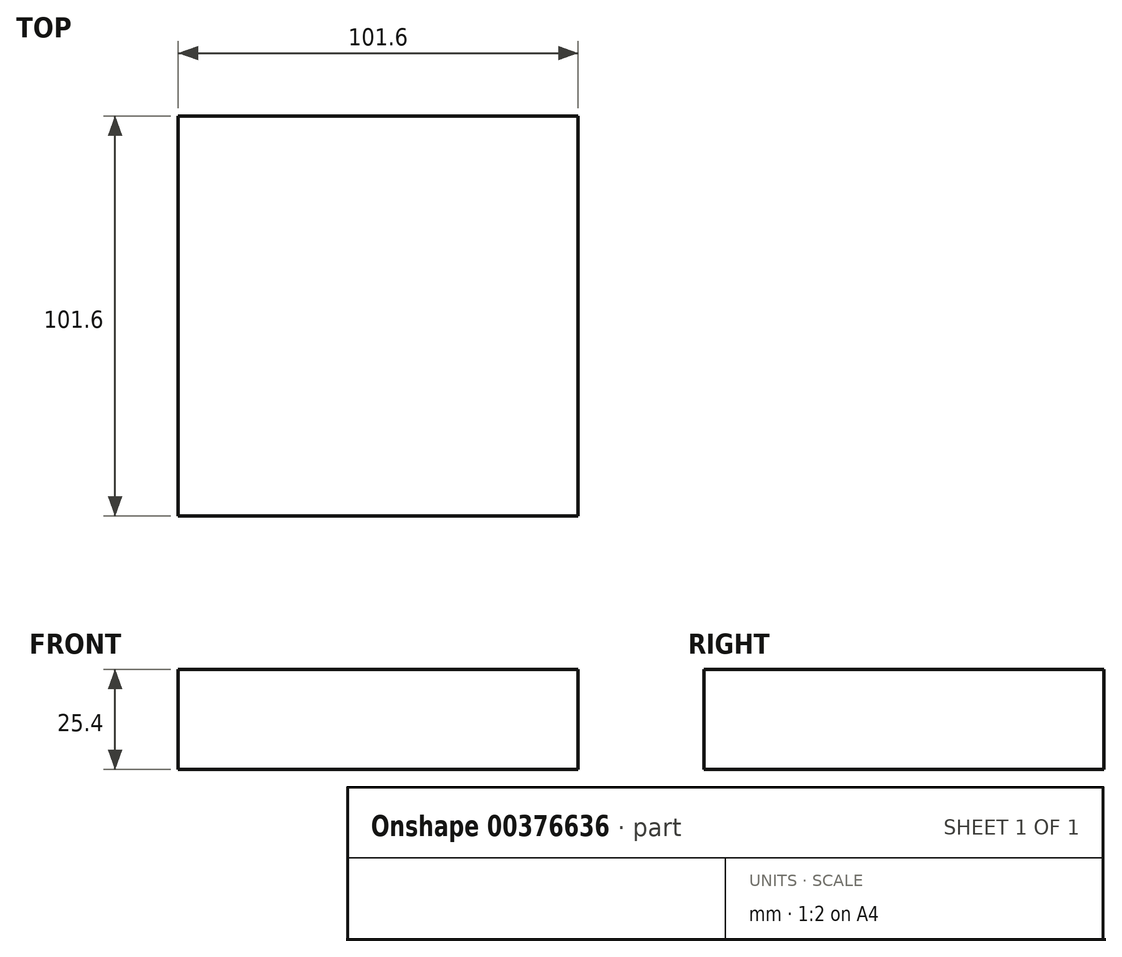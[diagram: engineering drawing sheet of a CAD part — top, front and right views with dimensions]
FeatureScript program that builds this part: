
annotation { "Feature Type Name" : "Feature", "Feature Type Description" : "" }
export const myFeature = defineFeature(function(context is Context, id is Id, definition is map)
    precondition{}
    {
        {
            var Q0;
            Q0=qCreatedBy(makeId("Top.planeOp"),FACE);
            var sketch = newSketch(context, id + "F0", { "sketchPlane" : qUnion([Q0])});
            skLineSegment(sketch, "E0.bottom", {"start": v(-50.8, 50.8) * mm, "end": v(50.8, 50.8) * mm});
            skLineSegment(sketch, "E0.top", {"start": v(-50.8, -50.8) * mm, "end": v(50.8, -50.8) * mm});
            skLineSegment(sketch, "E0.left", {"start": v(-50.8, 50.8) * mm, "end": v(-50.8, -50.8) * mm});
            skLineSegment(sketch, "E0.right", {"start": v(50.8, 50.8) * mm, "end": v(50.8, -50.8) * mm});
            skSolve(sketch);
        }
        {
            var Q0;
            Q0=makeQuery(id+"F0.imprint","IMPRINT",FACE,{"disambiguationData":[TD([[makeQuery(id+"F0.imprint","IMPRINT",EDGE,{"derivedFrom":sQuery(id+"F0.wireOp",EDGE,"E0.bottom")}),-1.0]])]});
            extrude(context, id + "F1", {"entities" : qUnion([Q0]), "depth" : 25.4 * mm});
        }
    });
